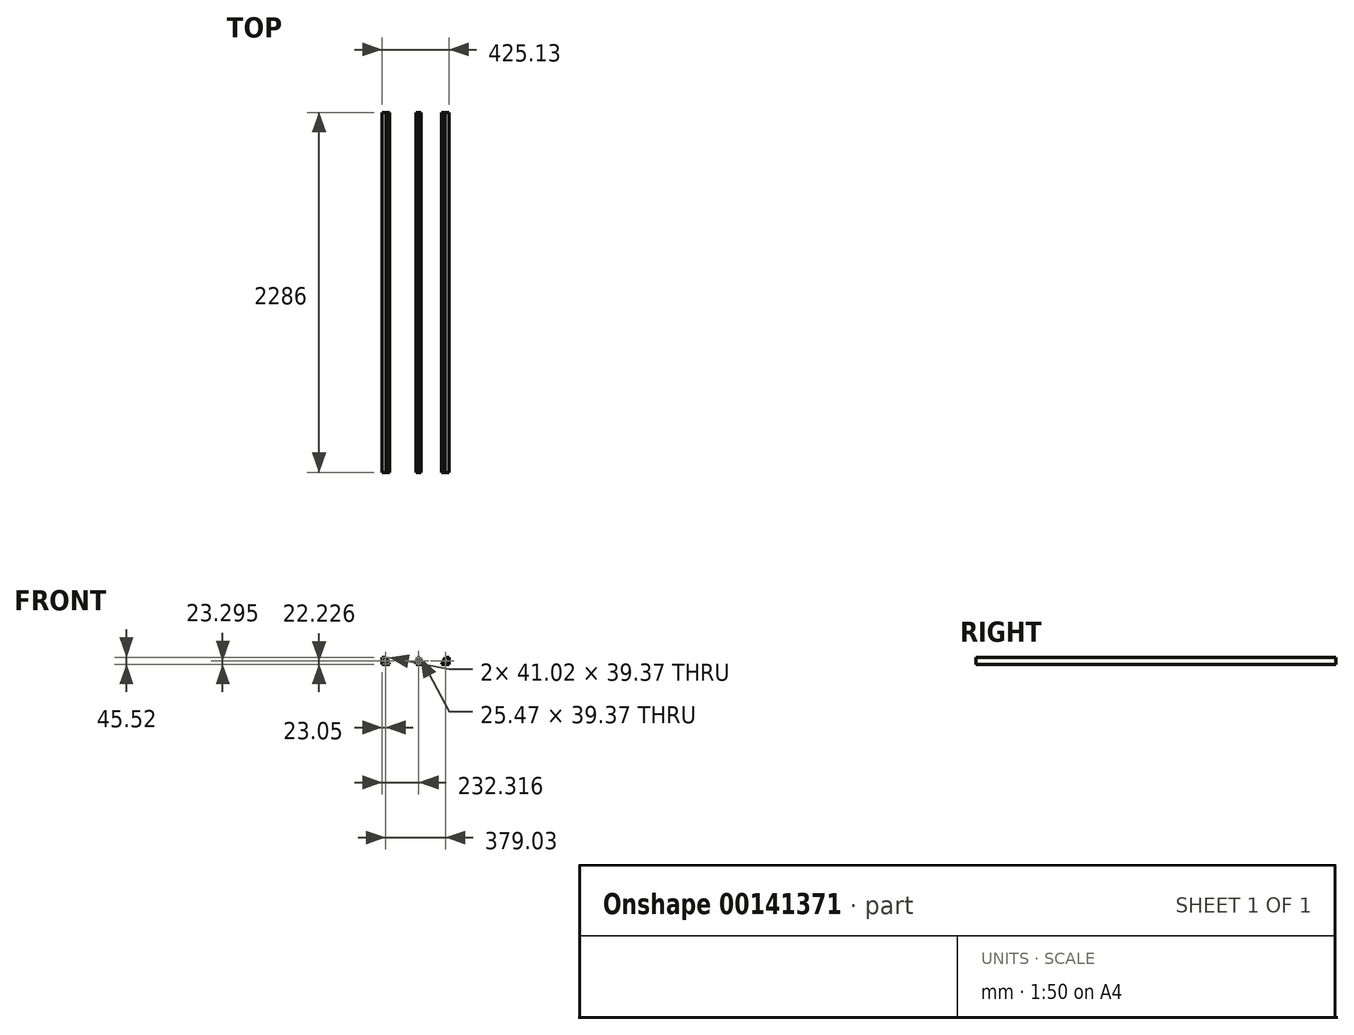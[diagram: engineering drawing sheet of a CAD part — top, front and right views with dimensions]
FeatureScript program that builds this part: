
annotation { "Feature Type Name" : "Feature", "Feature Type Description" : "" }
export const myFeature = defineFeature(function(context is Context, id is Id, definition is map)
    precondition{}
    {
        {
            var Q0;
            Q0=qCreatedBy(makeId("Front.planeOp"),FACE);
            var sketch = newSketch(context, id + "F0", { "sketchPlane" : qUnion([Q0])});
            skLineSegment(sketch, "E0.left", {"start": v(-203.31, 24.13) * mm, "end": v(-203.31, -20.32) * mm});
            skLineSegment(sketch, "E1", {"start": v(-203.31, 24.13) * mm, "end": v(-177.91, 24.13) * mm});
            skLineSegment(sketch, "E2", {"start": v(-177.91, 24.13) * mm, "end": v(-155.63, -20.32) * mm});
            skLineSegment(sketch, "E3", {"start": v(-155.63, -20.32) * mm, "end": v(-177.65, -20.32) * mm});
            skLineSegment(sketch, "E4", {"start": v(-177.65, -20.32) * mm, "end": v(-203.31, -20.32) * mm});
            skSolve(sketch);
        }
        {
            var Q0;
            Q0=makeQuery(id+"F0.imprint","IMPRINT",FACE,{"disambiguationData":[TD([[makeQuery(id+"F0.imprint","IMPRINT",EDGE,{"derivedFrom":sQuery(id+"F0.wireOp",EDGE,"E0.left")}),1.0]])]});
            extrude(context, id + "F1", {"entities" : qUnion([Q0]), "depth" : 2286 * mm});
        }
        {
            var Q0;
            Q0=makeQuery(id+"F1.opExtrude","CAP_FACE",FACE,{"disambiguationData":[OSD([sQuery(id+"F0.wireOp",EDGE,"E0.left"),sQuery(id+"F0.wireOp",EDGE,"E1"),sQuery(id+"F0.wireOp",EDGE,"E2"),sQuery(id+"F0.wireOp",EDGE,"E3"),sQuery(id+"F0.wireOp",EDGE,"E4")])],"isStart":false});
            var Q1;
            Q1=makeQuery(id+"F1.opExtrude","CAP_FACE",FACE,{"disambiguationData":[OSD([sQuery(id+"F0.wireOp",EDGE,"E0.left"),sQuery(id+"F0.wireOp",EDGE,"E1"),sQuery(id+"F0.wireOp",EDGE,"E2"),sQuery(id+"F0.wireOp",EDGE,"E3"),sQuery(id+"F0.wireOp",EDGE,"E4")])],"isStart":true});
            shell(context, id + "F2", {"entities" : qUnion([Q0, Q1]), "thickness" : 2.54 * mm});
        }
        {
            var Q0;
            Q0=qCreatedBy(makeId("Front.planeOp"),FACE);
            var sketch = newSketch(context, id + "F3", { "sketchPlane" : qUnion([Q0])});
            skLineSegment(sketch, "E5", {"start": v(13.13, -21.39) * mm, "end": v(22.66, 23.06) * mm});
            skLineSegment(sketch, "E6.MirrorCS", {"start": v(44.88, -21.39) * mm, "end": v(35.36, 23.06) * mm});
            skPoint(sketch, "E7.MirrorCS.start.orphan", {"position": v(44.88, -21.39) * mm});
            skLineSegment(sketch, "E8", {"start": v(13.13, -21.39) * mm, "end": v(44.88, -21.39) * mm});
            skLineSegment(sketch, "E9", {"start": v(35.36, 23.06) * mm, "end": v(22.66, 23.06) * mm});
            skSolve(sketch);
        }
        {
            var Q0;
            Q0=qCreatedBy(makeId("Front.planeOp"),FACE);
            var sketch = newSketch(context, id + "F4", { "sketchPlane" : qUnion([Q0])});
            skLineSegment(sketch, "E10.MirrorCS", {"start": v(221.82, 24.1) * mm, "end": v(221.82, -20.35) * mm});
            skLineSegment(sketch, "E11.MirrorCS", {"start": v(196.42, 24.1) * mm, "end": v(174.15, -20.35) * mm});
            skLineSegment(sketch, "E12.MirrorCS", {"start": v(221.82, 24.1) * mm, "end": v(196.42, 24.1) * mm});
            skLineSegment(sketch, "E13.MirrorCS", {"start": v(221.82, -20.35) * mm, "end": v(174.15, -20.35) * mm});
            skSolve(sketch);
        }
        {
            var Q0;
            Q0=makeQuery(id+"F3.imprint","IMPRINT",FACE,{"disambiguationData":[TD([[makeQuery(id+"F3.imprint","IMPRINT",EDGE,{"derivedFrom":sQuery(id+"F3.wireOp",EDGE,"E5")}),-1.0]])]});
            extrude(context, id + "F5", {"entities" : qUnion([Q0]), "depth" : 2286 * mm});
        }
        {
            var Q0;
            Q0=makeQuery(id+"F5.opExtrude","CAP_FACE",FACE,{"disambiguationData":[OSD([sQuery(id+"F3.wireOp",EDGE,"E5"),sQuery(id+"F3.wireOp",EDGE,"E6.MirrorCS"),sQuery(id+"F3.wireOp",EDGE,"E8"),sQuery(id+"F3.wireOp",EDGE,"E9")])],"isStart":true});
            var Q1;
            Q1=makeQuery(id+"F5.opExtrude","CAP_FACE",FACE,{"disambiguationData":[OSD([sQuery(id+"F3.wireOp",EDGE,"E5"),sQuery(id+"F3.wireOp",EDGE,"E6.MirrorCS"),sQuery(id+"F3.wireOp",EDGE,"E8"),sQuery(id+"F3.wireOp",EDGE,"E9")])],"isStart":false});
            shell(context, id + "F6", {"entities" : qUnion([Q0, Q1]), "thickness" : 2.54 * mm});
        }
        {
            var Q0;
            Q0=makeQuery(id+"F4.imprint","IMPRINT",FACE,{"disambiguationData":[TD([[makeQuery(id+"F4.imprint","IMPRINT",EDGE,{"derivedFrom":sQuery(id+"F4.wireOp",EDGE,"E10.MirrorCS")}),-1.0]])]});
            extrude(context, id + "F7", {"entities" : qUnion([Q0]), "depth" : 2286 * mm});
        }
        {
            var Q0;
            Q0=makeQuery(id+"F7.opExtrude","CAP_FACE",FACE,{"disambiguationData":[OSD([sQuery(id+"F4.wireOp",EDGE,"E10.MirrorCS"),sQuery(id+"F4.wireOp",EDGE,"E11.MirrorCS"),sQuery(id+"F4.wireOp",EDGE,"E12.MirrorCS"),sQuery(id+"F4.wireOp",EDGE,"E13.MirrorCS")])],"isStart":false});
            var Q1;
            Q1=makeQuery(id+"F7.opExtrude","CAP_FACE",FACE,{"disambiguationData":[OSD([sQuery(id+"F4.wireOp",EDGE,"E10.MirrorCS"),sQuery(id+"F4.wireOp",EDGE,"E11.MirrorCS"),sQuery(id+"F4.wireOp",EDGE,"E12.MirrorCS"),sQuery(id+"F4.wireOp",EDGE,"E13.MirrorCS")])],"isStart":true});
            shell(context, id + "F8", {"entities" : qUnion([Q0, Q1]), "thickness" : 2.54 * mm});
        }
    });
